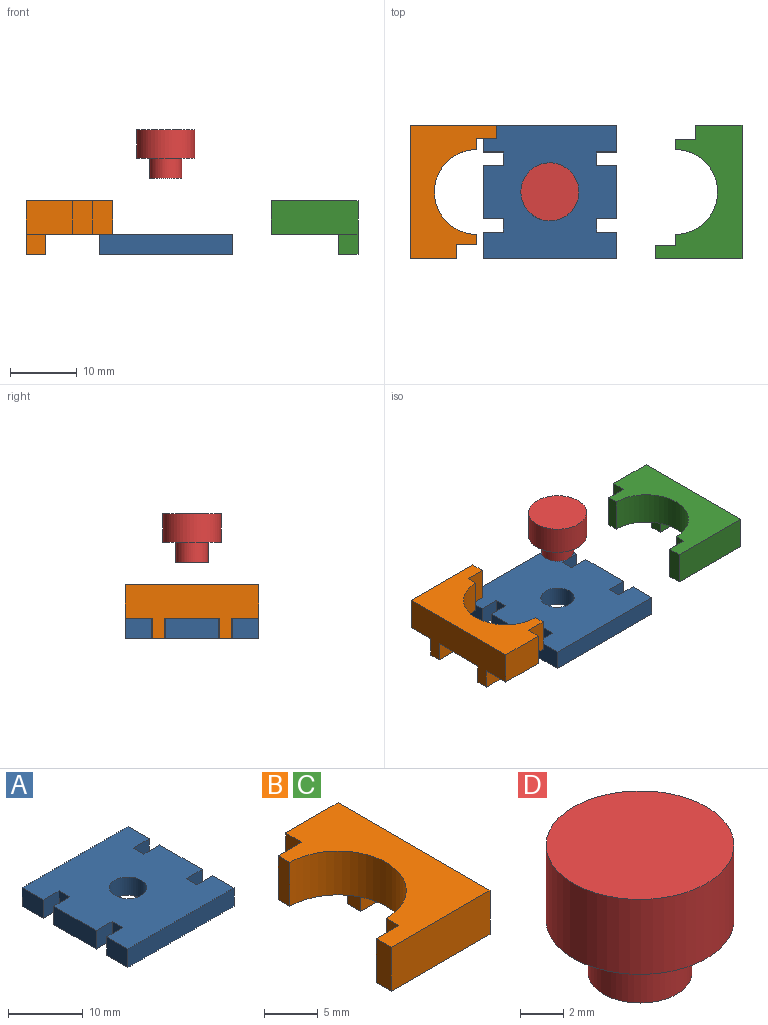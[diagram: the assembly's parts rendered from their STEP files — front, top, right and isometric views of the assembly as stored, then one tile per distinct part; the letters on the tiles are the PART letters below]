
ASSEMBLY  parts=4 mates=3
PART A: 23 faces, bbox 20x20x3 mm
  f0: plane 4x3mm, normal (1,0,0), area 12mm2, adj f7,f9,f10,f16
  f1: plane 8x3mm, normal (1,0,0), area 24mm2, adj f9,f10,f13,f14
  f2: plane 8x3mm, normal (-1,0,0), area 24mm2, adj f9,f10,f19,f20
  f3: plane 4x3mm, normal (-1,0,0), area 12mm2, adj f7,f9,f10,f17
  f4: plane 4x3mm, normal (1,0,0), area 12mm2, adj f5,f9,f10,f11
  f5: plane 20x3mm, normal (0,1,0), area 60mm2, adj f4,f6,f9,f10
  f6: plane 4x3mm, normal (-1,0,0), area 12mm2, adj f5,f9,f10,f22
  f7: plane 20x3mm, normal (0,-1,0), area 60mm2, adj f0,f3,f9,f10
  f8: cylinder r=2.5mm len=5mm, axis (0,0,-1), area 47.1mm2, adj f9,f10
  f9: plane 20x20mm, normal (0,0,1), area 356.4mm2, adj f0,f1,f2,f3,f4,f5,f6,f7
  f10: plane 20x20mm, normal (0,0,-1), area 356.4mm2, adj f0,f1,f2,f3,f4,f5,f6,f7
  f11: plane 3x3mm, normal (0,-1,0), area 9mm2, adj f4,f9,f10,f12
  f12: plane 3x2mm, normal (1,0,0), area 6mm2, adj f9,f10,f11,f13
  f13: plane 3x3mm, normal (0,1,0), area 9mm2, adj f1,f9,f10,f12
  f14: plane 3x3mm, normal (0,-1,0), area 9mm2, adj f1,f9,f10,f15
  f15: plane 3x2mm, normal (1,0,0), area 6mm2, adj f9,f10,f14,f16
  f16: plane 3x3mm, normal (0,1,0), area 9mm2, adj f0,f9,f10,f15
  f17: plane 3x3mm, normal (0,1,0), area 9mm2, adj f3,f9,f10,f18
  f18: plane 3x2mm, normal (-1,0,0), area 6mm2, adj f9,f10,f17,f19
  f19: plane 3x3mm, normal (0,-1,0), area 9mm2, adj f2,f9,f10,f18
  f20: plane 3x3mm, normal (0,1,0), area 9mm2, adj f2,f9,f10,f21
  f21: plane 3x2mm, normal (-1,0,0), area 6mm2, adj f9,f10,f20,f22
  f22: plane 3x3mm, normal (0,-1,0), area 9mm2, adj f6,f9,f10,f21
PART B: 20 faces, bbox 13x20x8 mm
  f0: plane 5x3.1mm, normal (0,1,0), area 15.5mm2, adj f1,f9,f10,f11
  f1: plane 5x1.55mm, normal (-1,0,0), area 7.8mm2, adj f0,f2,f10,f11
  f2: cylinder r=6.35mm len=12.7mm, axis (0,0,-1), area 99.7mm2, adj f1,f3,f10,f11
  f3: plane 5x1.65mm, normal (-1,0,0), area 8.3mm2, adj f2,f4,f10,f11
  f4: plane 5x3mm, normal (0,1,0), area 15mm2, adj f3,f5,f10,f11
  f5: plane 5x2mm, normal (-1,0,0), area 10mm2, adj f4,f6,f10,f11
  f6: plane 13x5mm, normal (0,-1,0), area 65mm2, adj f5,f7,f10,f11
  f7: plane 20x8mm, normal (1,0,0), area 110.8mm2, adj f6,f8,f10,f11,f12,f14,f15,f16
  f8: plane 6.9x5mm, normal (0,1,0), area 34.5mm2, adj f7,f9,f10,f11
  f9: plane 5x2.1mm, normal (-1,0,0), area 10.5mm2, adj f0,f8,f10,f11
  f10: plane 20x13mm, normal (0,0,1), area 136.2mm2, adj f0,f1,f2,f3,f4,f5,f6,f7
  f11: plane 20x13mm, normal (0,0,-1), area 125.7mm2, adj f0,f1,f2,f3,f4,f5,f6,f7
  f12: plane 3x2.9mm, normal (0,-1,0), area 8.7mm2, adj f7,f11,f13,f15
  f13: plane 3x1.8mm, normal (-1,0,0), area 5.4mm2, adj f11,f12,f14,f15
  f14: plane 3x2.9mm, normal (0,1,0), area 8.7mm2, adj f7,f11,f13,f15
  f15: plane 2.9x1.8mm, normal (0,0,-1), area 5.2mm2, adj f7,f12,f13,f14
  f16: plane 3x2.9mm, normal (0,-1,0), area 8.7mm2, adj f7,f11,f17,f19
  f17: plane 3x1.8mm, normal (-1,0,0), area 5.4mm2, adj f11,f16,f18,f19
  f18: plane 3x2.9mm, normal (0,1,0), area 8.7mm2, adj f7,f11,f17,f19
  f19: plane 2.9x1.8mm, normal (0,0,-1), area 5.2mm2, adj f7,f16,f17,f18
PART C: same geometry as B
PART D: 5 faces, bbox 8.7x8.7x7.3 mm
  f0: cylinder r=4.35mm len=8.7mm, axis (0,0,-1), area 116.2mm2, adj f1,f2
  f1: plane 8.7x8.7mm, normal (0,0,1), area 59.4mm2, adj f0
  f2: plane 8.7x8.7mm, normal (0,0,-1), area 41.4mm2, adj f0,f3
  f3: cylinder r=2.4mm len=4.8mm, axis (0,0,1), area 45.2mm2, adj f2,f4
  f4: plane 4.8x4.8mm, normal (0,0,-1), area 18.1mm2, adj f3
PLACE A t=(-1.53,-0.83,-1.42)mm fixed
PLACE B rot(axis=(0,0,1),180deg) t=(-12.5,-0.83,1.58)mm
PLACE C t=(17.25,-0.83,1.58)mm
PLACE D t=(-1.53,-0.83,12.96)mm
MATE slider A.f3 <-> B.f7  axis (-1,0,0) through (-11.53,-10.83,1.58)mm
MATE slider A.f0 <-> C.f7  axis (1,0,0) through (8.47,-10.83,1.58)mm
MATE slider A.f8 <-> D.f3  axis (0,0,-1) through (-1.53,-0.83,-1.42)mm
